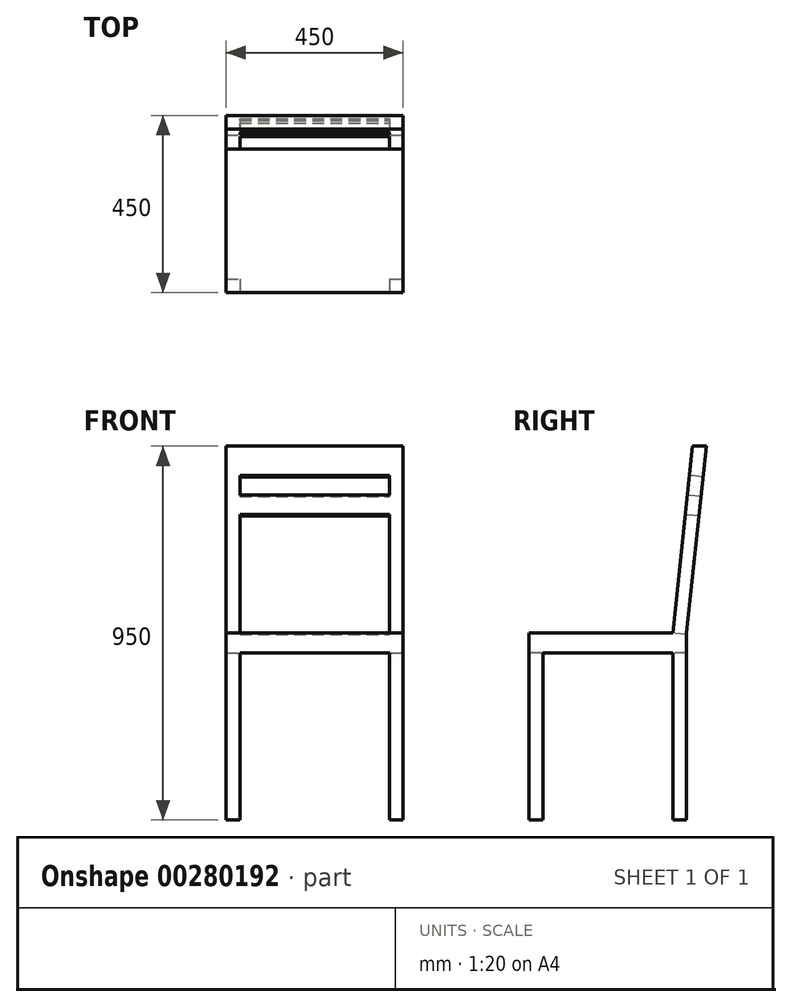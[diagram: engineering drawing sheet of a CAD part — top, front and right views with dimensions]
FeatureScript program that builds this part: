
annotation { "Feature Type Name" : "Feature", "Feature Type Description" : "" }
export const myFeature = defineFeature(function(context is Context, id is Id, definition is map)
    precondition{}
    {
        {
            var Q0;
            Q0=qCreatedBy(makeId("Top.planeOp"),FACE);
            var sketch = newSketch(context, id + "F0", { "sketchPlane" : qUnion([Q0])});
            skLineSegment(sketch, "E0.bottom", {"start": v(225, 225) * mm, "end": v(-225, 225) * mm});
            skLineSegment(sketch, "E0.top", {"start": v(225, -225) * mm, "end": v(-225, -225) * mm});
            skLineSegment(sketch, "E0.left", {"start": v(225, 225) * mm, "end": v(225, -225) * mm});
            skLineSegment(sketch, "E0.right", {"start": v(-225, 225) * mm, "end": v(-225, -225) * mm});
            skPoint(sketch, "E0.middle", {"position": v(0, 0) * mm});
            skSolve(sketch);
        }
        {
            var Q0;
            Q0=qSketchRegion(id+"F0",true);
            extrude(context, id + "F1", {"entities" : qUnion([Q0]), "depth" : 950 * mm});
        }
        {
            var Q0;
            Q0=makeQuery(id+"F1.opExtrude","SWEPT_FACE",FACE,{"disambiguationData":[OSD([sQuery(id+"F0.wireOp",EDGE,"E0.left")])]});
            var sketch = newSketch(context, id + "F2", { "sketchPlane" : qUnion([Q0])});
            skLineSegment(sketch, "E1.bottom", {"start": v(225, 475) * mm, "end": v(-225, 475) * mm});
            skLineSegment(sketch, "E1.top", {"start": v(225, 425) * mm, "end": v(-225, 425) * mm});
            skLineSegment(sketch, "E1.left", {"start": v(225, 475) * mm, "end": v(225, 425) * mm});
            skLineSegment(sketch, "E1.right", {"start": v(-225, 475) * mm, "end": v(-225, 425) * mm});
            skLineSegment(sketch, "E2", {"start": v(225, 950) * mm, "end": v(175, 475) * mm});
            skLineSegment(sketch, "E3", {"start": v(190, 950) * mm, "end": v(140, 475) * mm});
            skLineSegment(sketch, "E4", {"start": v(175, 475) * mm, "end": v(175, 0) * mm});
            skLineSegment(sketch, "E5", {"start": v(140, 475) * mm, "end": v(140, 0) * mm});
            skLineSegment(sketch, "E6", {"start": v(-225, 425) * mm, "end": v(-225, 0) * mm});
            skLineSegment(sketch, "E7", {"start": v(-190, 425) * mm, "end": v(-190, 0) * mm});
            skSolve(sketch);
        }
        {
            var Q0;
            {var subQ0=sQuery(id+"F2.wireOp",EDGE,"E7");Q0=makeQuery(id+"F2.imprint","IMPRINT",FACE,{"disambiguationData":[TD([[makeQuery(id+"F2.imprint","IMPRINT",EDGE,{"derivedFrom":subQ0}),1.0]])]});}
            var Q1;
            {var subQ1=sQuery(id+"F0.wireOp",EDGE,"E0.left");var subQ4=sQuery(id+"F2.wireOp",EDGE,"E4");var subQ6=makeQuery(id+"F1.opExtrude","CAP_EDGE",EDGE,{"disambiguationData":[OSD([subQ1])],"isStart":true});var subQ8=makeQuery(id+"F2.imprint","INTERSECT",VERTEX,{"derivedFrom":[subQ6,subQ4]});Q1=makeQuery(id+"F2.imprint","IMPRINT",FACE,{"disambiguationData":[TD([[makeQuery(id+"F2.imprint","IMPRINT",EDGE,{"disambiguationData":[TD([[subQ8,1.0]])],"derivedFrom":subQ4}),1.0]])]});}
            var Q2;
            {var subQ4=sQuery(id+"F2.wireOp",EDGE,"E2");Q2=makeQuery(id+"F2.imprint","IMPRINT",FACE,{"disambiguationData":[TD([[makeQuery(id+"F2.imprint","IMPRINT",EDGE,{"derivedFrom":subQ4}),1.0]])]});}
            var Q3;
            {var subQ0=sQuery(id+"F2.wireOp",EDGE,"E1.left");Q3=makeQuery(id+"F2.imprint","IMPRINT",FACE,{"disambiguationData":[TD([[makeQuery(id+"F2.imprint","IMPRINT",EDGE,{"derivedFrom":subQ0}),-1.0]])]});}
            var Q4;
            {var subQ4=sQuery(id+"F2.wireOp",EDGE,"E3");Q4=makeQuery(id+"F2.imprint","IMPRINT",FACE,{"disambiguationData":[TD([[makeQuery(id+"F2.imprint","IMPRINT",EDGE,{"derivedFrom":subQ4}),-1.0]])]});}
            extrude(context, id + "F3", {"entities" : qUnion([Q0, Q1, Q2, Q3, Q4]), "operationType" : NewBodyOperationType.REMOVE, "endBound" : BoundingType.THROUGH_ALL, "oppositeDirection" : true, "depth" : 25 * mm});
        }
        {
            var Q0;
            Q0=makeQuery(id+"F1.opExtrude","SWEPT_FACE",FACE,{"disambiguationData":[OSD([sQuery(id+"F0.wireOp",EDGE,"E0.top")])]});
            var sketch = newSketch(context, id + "F4", { "sketchPlane" : qUnion([Q0])});
            skLineSegment(sketch, "E8", {"start": v(-190, 0) * mm, "end": v(-190, 425) * mm});
            skLineSegment(sketch, "E9", {"start": v(-190, 425) * mm, "end": v(190, 425) * mm});
            skLineSegment(sketch, "E10", {"start": v(190, 425) * mm, "end": v(190, 0) * mm});
            skSolve(sketch);
        }
        {
            var Q0;
            {var subQ0=sQuery(id+"F4.wireOp",EDGE,"E8");Q0=makeQuery(id+"F4.imprint","IMPRINT",FACE,{"disambiguationData":[TD([[makeQuery(id+"F4.imprint","IMPRINT",EDGE,{"derivedFrom":subQ0}),-1.0]])]});}
            extrude(context, id + "F5", {"entities" : qUnion([Q0]), "operationType" : NewBodyOperationType.REMOVE, "endBound" : BoundingType.THROUGH_ALL, "oppositeDirection" : true, "depth" : 25 * mm});
        }
        {
            var Q0;
            Q0=makeQuery(id+"F3.boolean.opBoolean","COPY",FACE,{"derivedFrom":makeQuery(id+"F3.opExtrude","SWEPT_FACE",FACE,{"disambiguationData":[OSD([sQuery(id+"F2.wireOp",EDGE,"E3")])]})});
            var sketch = newSketch(context, id + "F6", { "sketchPlane" : qUnion([Q0])});
            skLineSegment(sketch, "E11", {"start": v(-190, 487.05) * mm, "end": v(-190, 889.67) * mm});
            skLineSegment(sketch, "E12", {"start": v(-190, 889.67) * mm, "end": v(190, 889.67) * mm});
            skLineSegment(sketch, "E13", {"start": v(190, 889.67) * mm, "end": v(190, 487.05) * mm});
            skLineSegment(sketch, "E14", {"start": v(-190, 839.67) * mm, "end": v(190, 839.67) * mm});
            skLineSegment(sketch, "E15", {"start": v(-190, 789.67) * mm, "end": v(190, 789.67) * mm});
            skSolve(sketch);
        }
        {
            var Q0;
            {var subQ0=sQuery(id+"F6.wireOp",EDGE,"E12");Q0=makeQuery(id+"F6.imprint","IMPRINT",FACE,{"disambiguationData":[TD([[makeQuery(id+"F6.imprint","IMPRINT",EDGE,{"derivedFrom":subQ0}),-1.0]])]});}
            var Q1;
            {var subQ3=sQuery(id+"F6.wireOp",EDGE,"E15");Q1=makeQuery(id+"F6.imprint","IMPRINT",FACE,{"disambiguationData":[TD([[makeQuery(id+"F6.imprint","IMPRINT",EDGE,{"derivedFrom":subQ3}),-1.0]])]});}
            extrude(context, id + "F7", {"entities" : qUnion([Q0, Q1]), "operationType" : NewBodyOperationType.REMOVE, "endBound" : BoundingType.THROUGH_ALL, "oppositeDirection" : true, "depth" : 25 * mm});
        }
    });
